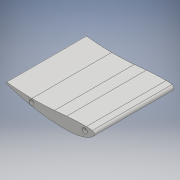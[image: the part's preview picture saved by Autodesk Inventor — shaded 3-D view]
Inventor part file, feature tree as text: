
AUTODESK INVENTOR PART (.ipt)
format: ipt  version: 2018 (Build 220112000, 112)  size: 275,456 bytes
history: native  units: mm
features: extrude x2, sketch x2, projected_geometry x1
ambient origin geometry x8: Origin, YZ Plane, XZ Plane, XY Plane, X Axis, Y Axis, Z Axis, Center Point
bodies: Body1 (feature_tree)
feature tree (5):
  extrude  "押し出し1"  Depth=112.5mm TaperAngle=0.0deg
  extrude  "押し出し2"  Depth=0.5mm
  sketch  "スケッチ1"
  projected_geometry  "投影ループ1"
  sketch  "スケッチ2"
